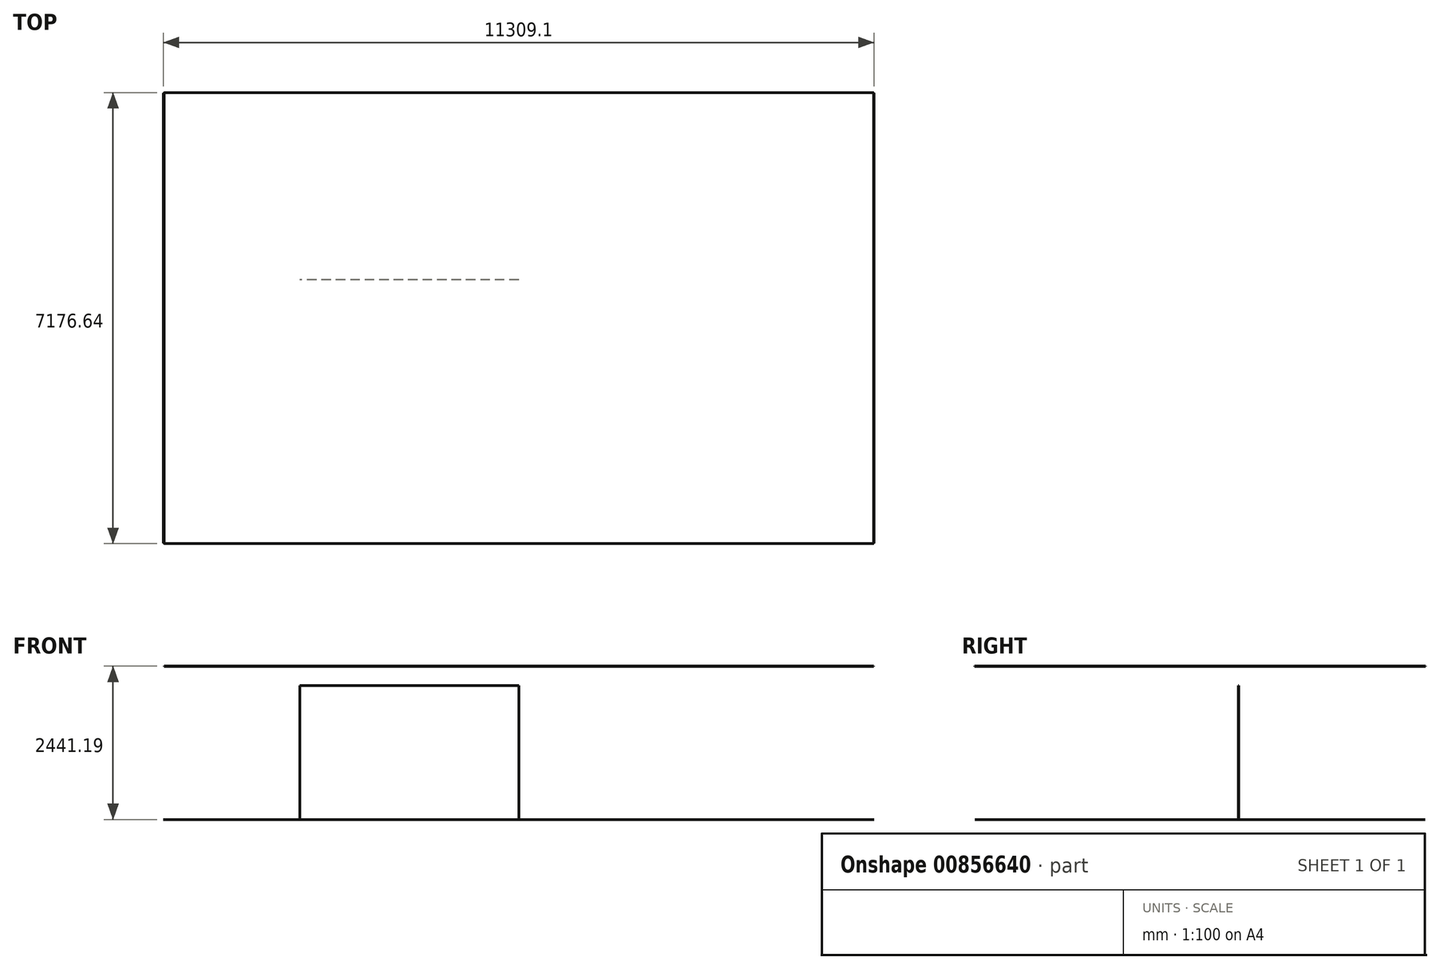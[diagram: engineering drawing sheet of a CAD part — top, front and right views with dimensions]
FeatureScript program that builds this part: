
annotation { "Feature Type Name" : "Feature", "Feature Type Description" : "" }
export const myFeature = defineFeature(function(context is Context, id is Id, definition is map)
    precondition{}
    {
        {
            var Q0;
            Q0=qCreatedBy(makeId("Front.planeOp"),FACE);
            var sketch = newSketch(context, id + "F0", { "sketchPlane" : qUnion([Q0])});
            skLineSegment(sketch, "E0.bottom", {"start": v(0, 0) * mm, "end": v(-3481.8, 0) * mm});
            skLineSegment(sketch, "E1.right", {"start": v(-3481.8, 2133.6) * mm, "end": v(-3481.8, 0) * mm});
            skLineSegment(sketch, "E2", {"start": v(0, 2133.6) * mm, "end": v(0, 0) * mm});
            skLineSegment(sketch, "E3", {"start": v(-3481.8, 2133.6) * mm, "end": v(0, 2133.6) * mm});
            skSolve(sketch);
        }
        {
            var Q0;
            Q0 = qSketchRegion(id + "F0", true);
            extrude(context, id + "F1", {"entities" : qUnion([Q0]), "oppositeDirection" : true, "depth" : 612.14 * mm, "offsetDistance" : 25.4 * mm, "hasSecondDirection" : true, "secondDirectionOppositeDirection" : false, "secondDirectionDepth" : -609.6 * mm});
        }
        {
            var Q0;
            Q0=qCreatedBy(makeId("Top.planeOp"),FACE);
            var sketch = newSketch(context, id + "F2", { "sketchPlane" : qUnion([Q0])});
            skLineSegment(sketch, "E4.bottom", {"start": v(5654.54, -3581.5) * mm, "end": v(-5654.54, -3581.5) * mm});
            skLineSegment(sketch, "E4.top", {"start": v(5654.54, 3581.5) * mm, "end": v(-5654.54, 3581.5) * mm});
            skLineSegment(sketch, "E4.left", {"start": v(5654.54, -3581.5) * mm, "end": v(5654.54, 3581.5) * mm});
            skLineSegment(sketch, "E4.right", {"start": v(-5654.54, -3581.5) * mm, "end": v(-5654.54, 3581.5) * mm});
            skPoint(sketch, "E4.middle", {"position": v(0, 0) * mm});
            skSolve(sketch);
        }
        {
            var Q0;
            Q0 = qSketchRegion(id + "F2", true);
            extrude(context, id + "F3", {"entities" : qUnion([Q0]), "oppositeDirection" : true, "depth" : 0.25 * mm, "offsetDistance" : 25.4 * mm});
        }
        {
            var Q0;
            Q0=qCreatedBy(makeId("Top.planeOp"),FACE);
            var sketch = newSketch(context, id + "F4", { "sketchPlane" : qUnion([Q0])});
            skLineSegment(sketch, "E5.bottom", {"start": v(5645.27, -3588.32) * mm, "end": v(-5645.27, -3588.32) * mm});
            skLineSegment(sketch, "E5.top", {"start": v(5645.27, 3588.32) * mm, "end": v(-5645.27, 3588.32) * mm});
            skLineSegment(sketch, "E5.left", {"start": v(5645.27, -3588.32) * mm, "end": v(5645.27, 3588.32) * mm});
            skLineSegment(sketch, "E5.right", {"start": v(-5645.27, -3588.32) * mm, "end": v(-5645.27, 3588.32) * mm});
            skPoint(sketch, "E5.middle", {"position": v(0, 0) * mm});
            skSolve(sketch);
        }
        {
            var Q0;
            Q0 = qSketchRegion(id + "F4", true);
            extrude(context, id + "F5", {"entities" : qUnion([Q0]), "depth" : 2440.94 * mm, "offsetDistance" : 25.4 * mm, "hasSecondDirection" : true, "secondDirectionOppositeDirection" : false, "secondDirectionDepth" : 2438.4 * mm});
        }
    });
